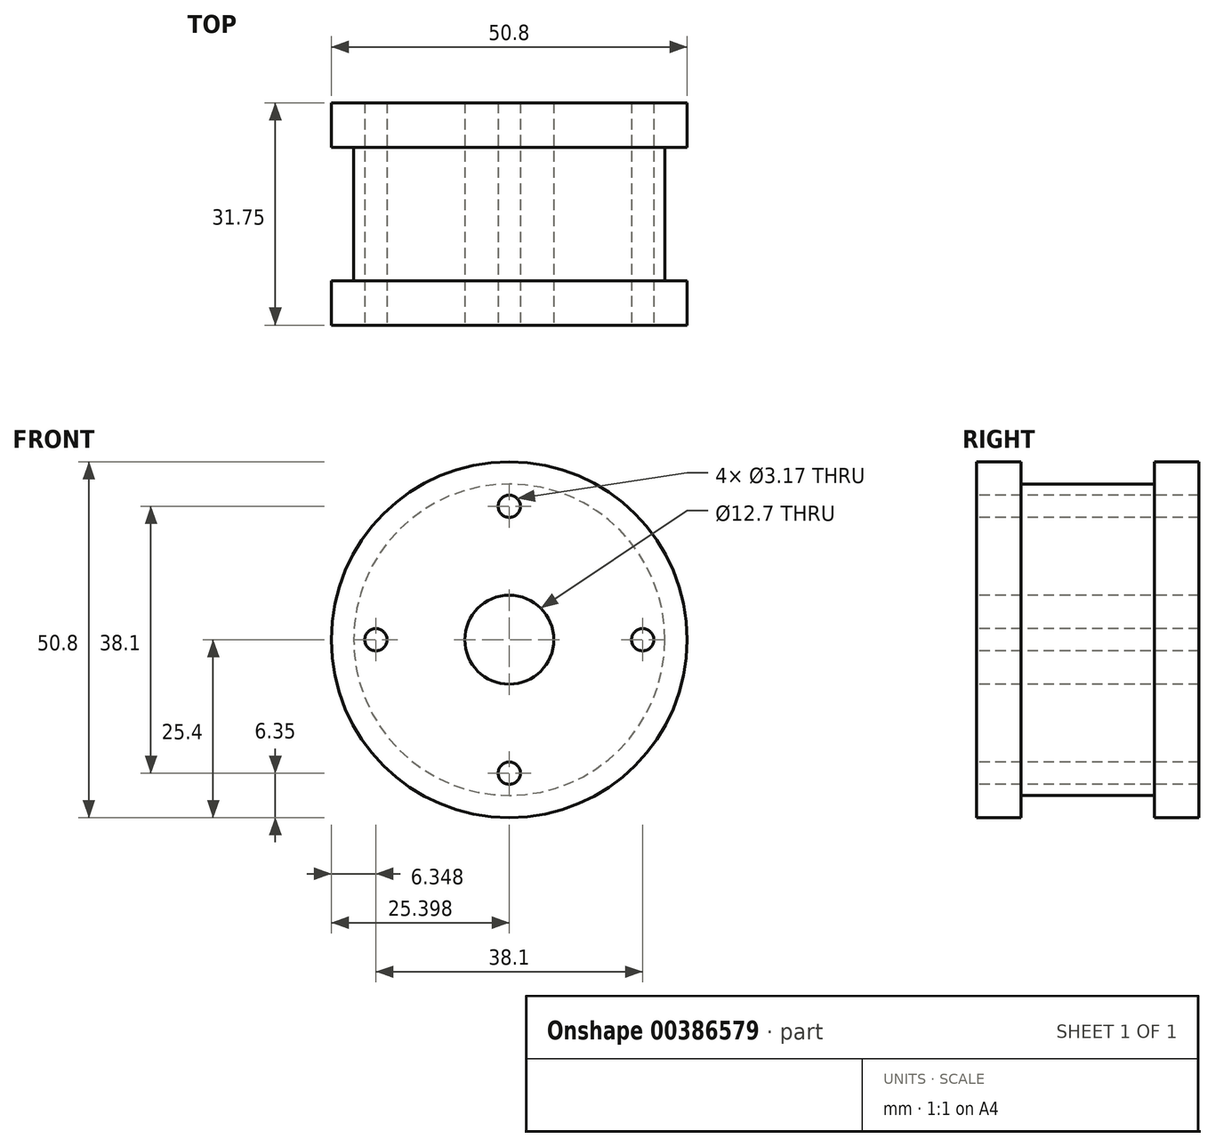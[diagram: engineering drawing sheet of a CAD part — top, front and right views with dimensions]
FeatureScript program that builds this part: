
annotation { "Feature Type Name" : "Feature", "Feature Type Description" : "" }
export const myFeature = defineFeature(function(context is Context, id is Id, definition is map)
    precondition{}
    {
        {
            var Q0;
            Q0=qCreatedBy(makeId("Front.planeOp"),FACE);
            var sketch = newSketch(context, id + "F0", { "sketchPlane" : qUnion([Q0])});
            skCircle(sketch, "E0", {"center": v(0.66, 0) * mm, "radius": 25.4 * mm});
            skCircle(sketch, "E1", {"center": v(0.66, 0) * mm, "radius": 22.23 * mm, "construction": true});
            skSolve(sketch);
        }
        {
            var Q0;
            Q0 = qSketchRegion(id + "F0", true);
            extrude(context, id + "F1", {"entities" : qUnion([Q0]), "depth" : 6.35 * mm});
        }
        {
            var Q0;
            Q0=makeQuery(id+"F1.opExtrude","CAP_FACE",FACE,{"disambiguationData":[OSD([sQuery(id+"F0.wireOp",EDGE,"E0")])],"isStart":false});
            var sketch = newSketch(context, id + "F2", { "sketchPlane" : qUnion([Q0])});
            skPoint(sketch, "E2", {"position": v(0, 0) * mm});
            skPoint(sketch, "E3", {"position": v(0, 19.04) * mm});
            skPoint(sketch, "E4", {"position": v(0, -19.04) * mm});
            skPoint(sketch, "E5", {"position": v(19.7, 0) * mm});
            skPoint(sketch, "E6", {"position": v(-18.4, 0) * mm});
            skSolve(sketch);
        }
        {
            var Q0;
            Q0=makeQuery(id+"F1.opExtrude","CAP_FACE",FACE,{"disambiguationData":[OSD([sQuery(id+"F0.wireOp",EDGE,"E0")])],"isStart":true});
            var sketch = newSketch(context, id + "F3", { "sketchPlane" : qUnion([Q0])});
            skCircle(sketch, "E7", {"center": v(-0.66, 0) * mm, "radius": 22.23 * mm});
            skSolve(sketch);
        }
        {
            var Q0;
            Q0 = qSketchRegion(id + "F3", true);
            extrude(context, id + "F4", {"entities" : qUnion([Q0]), "operationType" : NewBodyOperationType.ADD, "depth" : 19.05 * mm});
        }
        {
            var Q0;
            Q0=makeQuery(id+"F4.opExtrude","CAP_FACE",FACE,{"disambiguationData":[OSD([sQuery(id+"F3.wireOp",EDGE,"E7")])],"isStart":false});
            var sketch = newSketch(context, id + "F5", { "sketchPlane" : qUnion([Q0])});
            skCircle(sketch, "E8", {"center": v(-0.66, 0) * mm, "radius": 25.4 * mm});
            skSolve(sketch);
        }
        {
            var Q0;
            Q0 = qSketchRegion(id + "F5", true);
            extrude(context, id + "F6", {"entities" : qUnion([Q0]), "operationType" : NewBodyOperationType.ADD, "depth" : 6.35 * mm});
        }
        {
            var Q0;
            Q0=makeQuery(id+"F1.opExtrude","CAP_FACE",FACE,{"disambiguationData":[OSD([sQuery(id+"F0.wireOp",EDGE,"E0")])],"isStart":false});
            var sketch = newSketch(context, id + "F7", { "sketchPlane" : qUnion([Q0])});
            skPoint(sketch, "E9", {"position": v(0.66, 0) * mm});
            skPoint(sketch, "E10", {"position": v(0.66, 19.05) * mm});
            skPoint(sketch, "E11", {"position": v(19.7, 0) * mm});
            skPoint(sketch, "E12", {"position": v(0.66, -19.05) * mm});
            skPoint(sketch, "E13", {"position": v(-18.4, 0) * mm});
            skSolve(sketch);
        }
        {
            var Q0;
            Q0=sQuery(id+"F7.wireOp",VERTEX,"E10");
            var Q1;
            Q1=sQuery(id+"F7.wireOp",VERTEX,"E11");
            var Q2;
            Q2=sQuery(id+"F7.wireOp",VERTEX,"E12");
            var Q3;
            Q3=sQuery(id+"F7.wireOp",VERTEX,"E13");
            var Q4;
            Q4=makeQuery(id+"F1.opExtrude","SWEPT_BODY",BODY,{"disambiguationData":[OSD([sQuery(id+"F0.wireOp",EDGE,"E0")])]});
            hole(context, id + "F8", {"style" : HoleStyle.SIMPLE, "endStyle" : HoleEndStyle.THROUGH, "holeDiameter" : 3.17 * mm, "isTappedThrough" : true, "tappedDepth" : 12.7 * mm, "tapClearance" : 3, "locations" : qUnion([Q0, Q1, Q2, Q3]), "scope" : qUnion([Q4])});
        }
        {
            var Q0;
            Q0=sQuery(id+"F7.wireOp",VERTEX,"E9");
            var Q1;
            Q1=makeQuery(id+"F1.opExtrude","SWEPT_BODY",BODY,{"disambiguationData":[OSD([sQuery(id+"F0.wireOp",EDGE,"E0")])]});
            hole(context, id + "F9", {"style" : HoleStyle.SIMPLE, "endStyle" : HoleEndStyle.THROUGH, "holeDiameter" : 12.7 * mm, "isTappedThrough" : true, "tappedDepth" : 12.7 * mm, "tapClearance" : 3, "locations" : qUnion([Q0]), "scope" : qUnion([Q1])});
        }
    });
